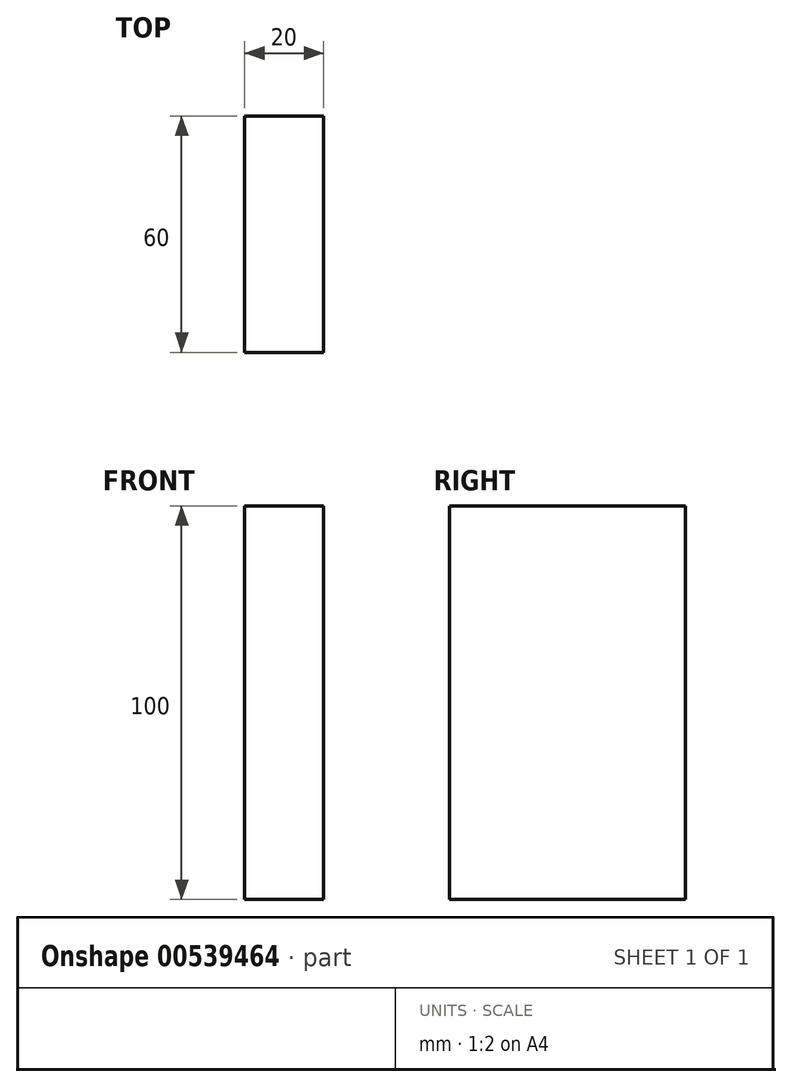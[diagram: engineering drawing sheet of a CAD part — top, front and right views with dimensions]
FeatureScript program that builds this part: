
annotation { "Feature Type Name" : "Feature", "Feature Type Description" : "" }
export const myFeature = defineFeature(function(context is Context, id is Id, definition is map)
    precondition{}
    {
        {
            var Q0;
            Q0=qCreatedBy(makeId("Right.planeOp"),FACE);
            var sketch = newSketch(context, id + "F0", { "sketchPlane" : qUnion([Q0])});
            skLineSegment(sketch, "E0.bottom", {"start": v(0, 61.77) * mm, "end": v(60, 61.77) * mm});
            skLineSegment(sketch, "E0.top", {"start": v(0, -38.23) * mm, "end": v(60, -38.23) * mm});
            skLineSegment(sketch, "E0.left", {"start": v(0, 61.77) * mm, "end": v(0, -38.23) * mm});
            skLineSegment(sketch, "E0.right", {"start": v(60, 61.77) * mm, "end": v(60, -38.23) * mm});
            skSolve(sketch);
        }
        {
            var Q0;
            Q0=makeQuery(id+"F0.imprint","IMPRINT",FACE,{"disambiguationData":[TD([[makeQuery(id+"F0.imprint","IMPRINT",EDGE,{"derivedFrom":sQuery(id+"F0.wireOp",EDGE,"E0.bottom")}),-1.0]])]});
            extrude(context, id + "F1", {"entities" : qUnion([Q0]), "depth" : 20 * mm, "offsetDistance" : 25 * mm});
        }
    });
